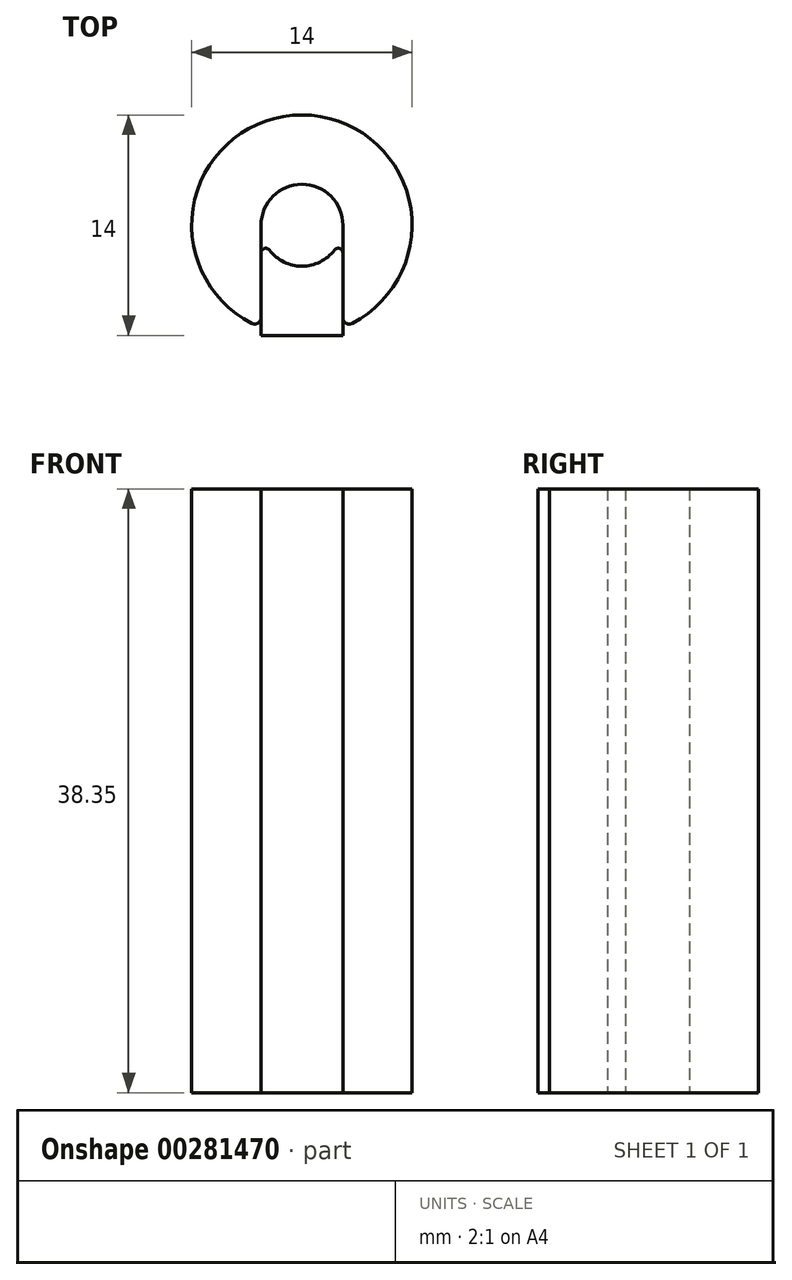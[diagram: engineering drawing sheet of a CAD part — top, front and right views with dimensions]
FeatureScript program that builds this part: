
annotation { "Feature Type Name" : "Feature", "Feature Type Description" : "" }
export const myFeature = defineFeature(function(context is Context, id is Id, definition is map)
    precondition{}
    {
        {
            var Q0;
            Q0=qCreatedBy(makeId("Top.planeOp"),FACE);
            var sketch = newSketch(context, id + "F0", { "sketchPlane" : qUnion([Q0])});
            skCircle(sketch, "E0", {"center": v(0, 0) * mm, "radius": 2.6 * mm});
            skArc(sketch, "E1", {"start": v(2.6, -6.5) * mm, "mid": v(0, 7) * mm, "end": v(-2.6, -6.5) * mm});
            skLineSegment(sketch, "E2", {"start": v(2.6, 0) * mm, "end": v(2.6, -7) * mm});
            skLineSegment(sketch, "E3", {"start": v(-2.6, 0) * mm, "end": v(-2.6, -7) * mm});
            skLineSegment(sketch, "E4", {"start": v(0, -7) * mm, "end": v(-2.6, -7) * mm});
            skLineSegment(sketch, "E5", {"start": v(-2.6, -7) * mm, "end": v(2.6, -7) * mm});
            skSolve(sketch);
        }
        {
            var Q0;
            {var subQ5=sQuery(id+"F0.wireOp",EDGE,"E1");Q0=makeQuery(id+"F0.imprint","IMPRINT",FACE,{"disambiguationData":[TD([[makeQuery(id+"F0.imprint","IMPRINT",EDGE,{"derivedFrom":subQ5}),1.0]])]});}
            extrude(context, id + "F1", {"entities" : qUnion([Q0]), "depth" : 38.35 * mm});
        }
        {
            var Q0;
            {var subQ3=sQuery(id+"F0.wireOp",EDGE,"E0");var subQ5=sQuery(id+"F0.wireOp",EDGE,"E2");var subQ9=makeQuery(id+"F0.imprint","INTERSECT",VERTEX,{"derivedFrom":[subQ3,subQ5]});Q0=makeQuery(id+"F0.imprint","IMPRINT",FACE,{"disambiguationData":[TD([[makeQuery(id+"F0.imprint","IMPRINT",EDGE,{"disambiguationData":[TD([[subQ9,1.0]])],"derivedFrom":subQ3}),-1.0]])]});}
            extrude(context, id + "F2", {"entities" : qUnion([Q0]), "depth" : 38.35 * mm});
        }
        {
            var Q0;
            Q0=makeQuery(id+"F2.opExtrude","SWEPT_EDGE",EDGE,{"disambiguationData":[OSD([sQuery(id+"F0.wireOp",EDGE,"E0"),sQuery(id+"F0.wireOp",EDGE,"E3")])]});
            var Q1;
            Q1=makeQuery(id+"F2.opExtrude","SWEPT_EDGE",EDGE,{"disambiguationData":[OSD([sQuery(id+"F0.wireOp",EDGE,"E0"),sQuery(id+"F0.wireOp",EDGE,"E2")])]});
            fillet(context, id + "F3", {"entities" : qUnion([Q0, Q1]), "radius" : 0.3 * mm, "tangentPropagation" : true, "allowEdgeOverflow" : false});
        }
        {
            var Q0;
            Q0=makeQuery(id+"F1.opExtrude","SWEPT_EDGE",EDGE,{"disambiguationData":[OSD([sQuery(id+"F0.wireOp",EDGE,"E1"),sQuery(id+"F0.wireOp",EDGE,"E3")])]});
            var Q1;
            Q1=makeQuery(id+"F1.opExtrude","SWEPT_EDGE",EDGE,{"disambiguationData":[OSD([sQuery(id+"F0.wireOp",EDGE,"E1"),sQuery(id+"F0.wireOp",EDGE,"E2")])]});
            fillet(context, id + "F4", {"entities" : qUnion([Q0, Q1]), "radius" : 0.4 * mm, "tangentPropagation" : true, "allowEdgeOverflow" : false});
        }
    });
